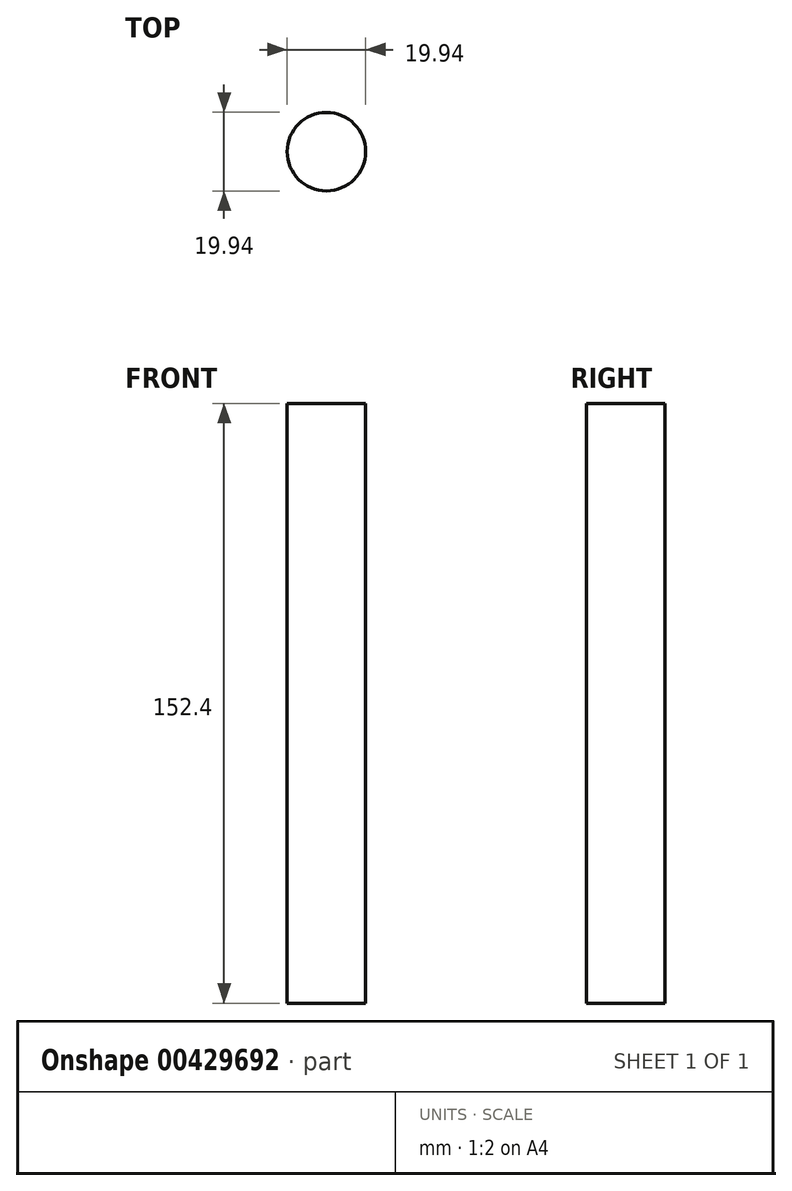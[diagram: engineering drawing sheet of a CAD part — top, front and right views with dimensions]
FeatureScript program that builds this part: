
annotation { "Feature Type Name" : "Feature", "Feature Type Description" : "" }
export const myFeature = defineFeature(function(context is Context, id is Id, definition is map)
    precondition{}
    {
        {
            var Q0;
            Q0=qCreatedBy(makeId("Top.planeOp"),FACE);
            var sketch = newSketch(context, id + "F0", { "sketchPlane" : qUnion([Q0])});
            skCircle(sketch, "E0", {"center": v(-61.61, -37.72) * mm, "radius": 9.97 * mm});
            skSolve(sketch);
        }
        {
            var Q0;
            Q0=qSketchRegion(id+"F0",true);
            extrude(context, id + "F1", {"entities" : qUnion([Q0]), "depth" : 152.4 * mm});
        }
    });
